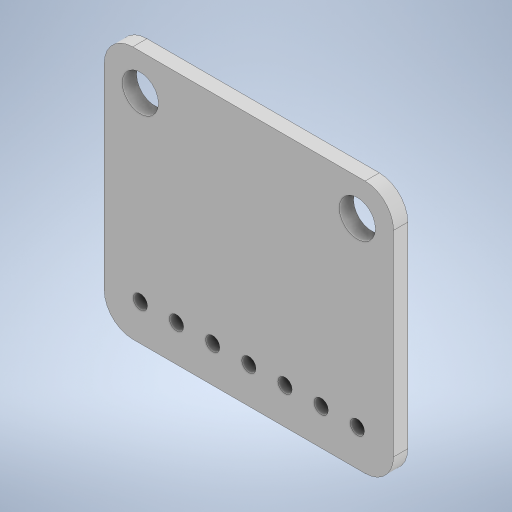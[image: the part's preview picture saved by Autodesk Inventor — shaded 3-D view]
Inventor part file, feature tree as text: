
AUTODESK INVENTOR PART (.ipt)
format: ipt  version: 2023 (Build 270158000, 158)  size: 276,992 bytes
history: native  units: mm
features: extrude x1, sketch x1
ambient origin geometry x8: Origin, YZ Plane, XZ Plane, XY Plane, X Axis, Y Axis, Z Axis, Center Point
bodies: Solid1 (feature_tree)
feature tree (2):
  extrude  "Extrusion1"  Depth=17.78mm
  sketch  "Sketch1"  dims[d0=20.32mm d1=17.78mm d2=15.24mm d3=2.54mm d4=2.54mm d5=2.0mm d6=1.0mm d7=0.0mm d8=2.54mm d9=1.0mm d10=40.0mm d12=2.54mm d13=40.0mm d15=2.54mm]
